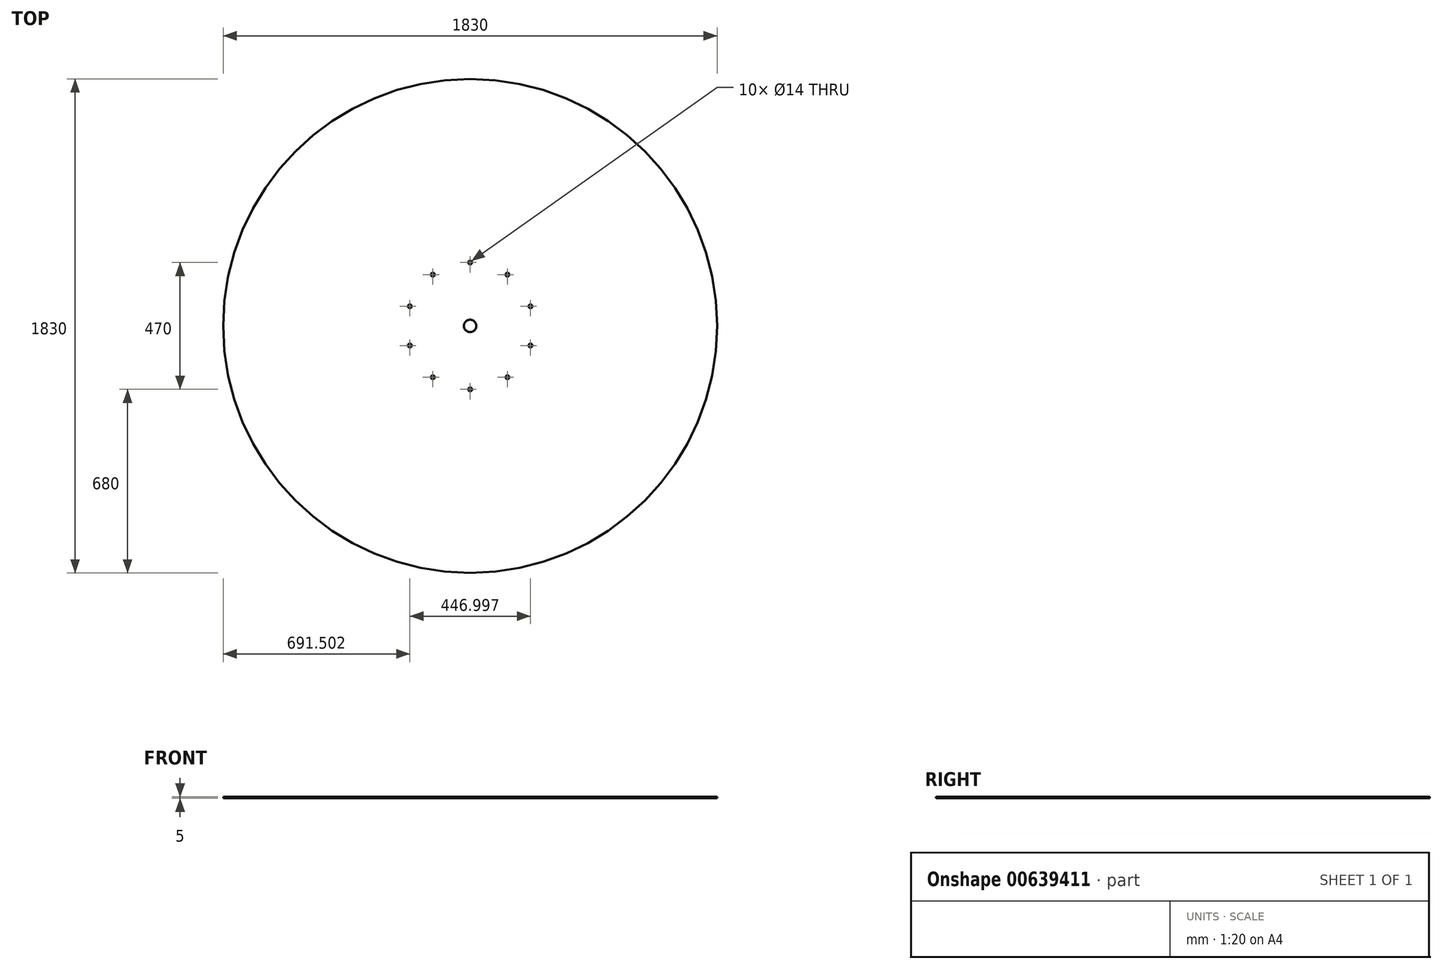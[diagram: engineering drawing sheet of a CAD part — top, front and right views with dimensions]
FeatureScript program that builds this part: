
annotation { "Feature Type Name" : "Feature", "Feature Type Description" : "" }
export const myFeature = defineFeature(function(context is Context, id is Id, definition is map)
    precondition{}
    {
        {
            var Q0;
            Q0=qCreatedBy(makeId("Top.planeOp"),FACE);
            var sketch = newSketch(context, id + "F0", { "sketchPlane" : qUnion([Q0])});
            skCircle(sketch, "E0", {"center": v(0, 0) * mm, "radius": 915 * mm});
            skCircle(sketch, "E1", {"center": v(0, 0) * mm, "radius": 235 * mm, "construction": true});
            skCircle(sketch, "E2", {"center": v(0, 235) * mm, "radius": 7 * mm});
            skCircle(sketch, "E3.1.0", {"center": v(-138.13, 190.12) * mm, "radius": 7 * mm});
            skCircle(sketch, "E3.2.0", {"center": v(-223.5, 72.62) * mm, "radius": 7 * mm});
            skCircle(sketch, "E3.3.0", {"center": v(-223.5, -72.62) * mm, "radius": 7 * mm});
            skCircle(sketch, "E3.4.0", {"center": v(-138.13, -190.12) * mm, "radius": 7 * mm});
            skCircle(sketch, "E3.5.0", {"center": v(0, -235) * mm, "radius": 7 * mm});
            skCircle(sketch, "E3.6.0", {"center": v(138.13, -190.12) * mm, "radius": 7 * mm});
            skCircle(sketch, "E3.7.0", {"center": v(223.5, -72.62) * mm, "radius": 7 * mm});
            skCircle(sketch, "E3.8.0", {"center": v(223.5, 72.62) * mm, "radius": 7 * mm});
            skCircle(sketch, "E3.9.0", {"center": v(138.13, 190.12) * mm, "radius": 7 * mm});
            skCircle(sketch, "E4", {"center": v(0, 0) * mm, "radius": 23 * mm});
            skSolve(sketch);
        }
        {
            var Q0;
            Q0=makeQuery(id+"F0.imprint","IMPRINT",FACE,{"disambiguationData":[TD([[makeQuery(id+"F0.imprint","IMPRINT",EDGE,{"derivedFrom":sQuery(id+"F0.wireOp",EDGE,"E0")}),1.0]])]});
            extrude(context, id + "F1", {"entities" : qUnion([Q0]), "depth" : 5 * mm, "offsetDistance" : 25 * mm});
        }
    });
